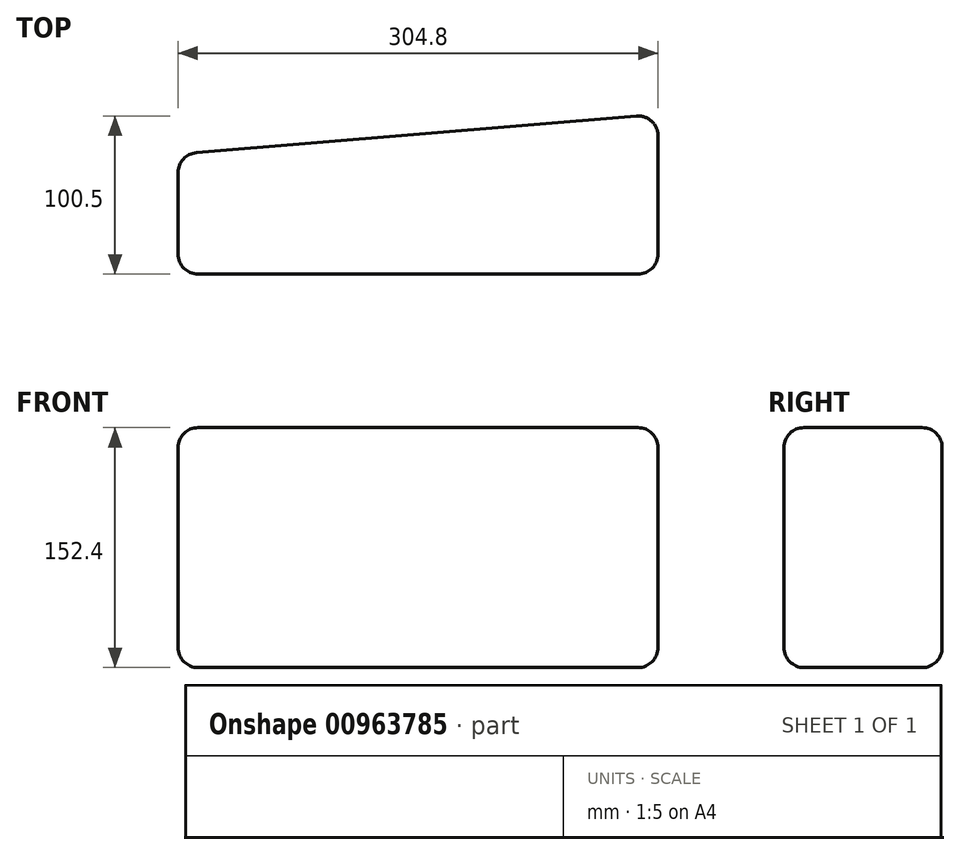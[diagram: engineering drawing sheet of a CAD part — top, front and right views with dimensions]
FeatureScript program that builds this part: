
annotation { "Feature Type Name" : "Feature", "Feature Type Description" : "" }
export const myFeature = defineFeature(function(context is Context, id is Id, definition is map)
    precondition{}
    {
        {
            var Q0;
            Q0=qCreatedBy(makeId("Top.planeOp"),FACE);
            var sketch = newSketch(context, id + "F0", { "sketchPlane" : qUnion([Q0])});
            skLineSegment(sketch, "E0", {"start": v(0, 0) * mm, "end": v(0, 76.2) * mm});
            skLineSegment(sketch, "E1", {"start": v(0, 76.2) * mm, "end": v(304.8, 101.6) * mm});
            skLineSegment(sketch, "E2", {"start": v(304.8, 101.6) * mm, "end": v(304.8, 0) * mm});
            skLineSegment(sketch, "E3", {"start": v(304.8, 0) * mm, "end": v(0, 0) * mm});
            skSolve(sketch);
        }
        {
            var Q0;
            Q0 = qSketchRegion(id + "F0", true);
            extrude(context, id + "F1", {"entities" : qUnion([Q0]), "depth" : 152.4 * mm, "offsetDistance" : 25.4 * mm});
        }
        {
            var Q0;
            Q0=makeQuery(id+"F1.opExtrude","CAP_EDGE",EDGE,{"disambiguationData":[OSD([sQuery(id+"F0.wireOp",EDGE,"E2")])],"isStart":false});
            var Q1;
            Q1=makeQuery(id+"F1.opExtrude","SWEPT_EDGE",EDGE,{"disambiguationData":[OSD([sQuery(id+"F0.wireOp",EDGE,"E0"),sQuery(id+"F0.wireOp",EDGE,"E1")])]});
            var Q2;
            Q2=makeQuery(id+"F1.opExtrude","CAP_EDGE",EDGE,{"disambiguationData":[OSD([sQuery(id+"F0.wireOp",EDGE,"E1")])],"isStart":false});
            var Q3;
            Q3=makeQuery(id+"F1.opExtrude","CAP_EDGE",EDGE,{"disambiguationData":[OSD([sQuery(id+"F0.wireOp",EDGE,"E0")])],"isStart":false});
            var Q4;
            Q4=makeQuery(id+"F1.opExtrude","SWEPT_EDGE",EDGE,{"disambiguationData":[OSD([sQuery(id+"F0.wireOp",EDGE,"E2"),sQuery(id+"F0.wireOp",EDGE,"E3")])]});
            var Q5;
            Q5=makeQuery(id+"F1.opExtrude","CAP_EDGE",EDGE,{"disambiguationData":[OSD([sQuery(id+"F0.wireOp",EDGE,"E3")])],"isStart":false});
            var Q6;
            Q6=makeQuery(id+"F1.opExtrude","SWEPT_EDGE",EDGE,{"disambiguationData":[OSD([sQuery(id+"F0.wireOp",EDGE,"E1"),sQuery(id+"F0.wireOp",EDGE,"E2")])]});
            var Q7;
            Q7=makeQuery(id+"F1.opExtrude","CAP_EDGE",EDGE,{"disambiguationData":[OSD([sQuery(id+"F0.wireOp",EDGE,"E2")])],"isStart":true});
            var Q8;
            Q8=makeQuery(id+"F1.opExtrude","SWEPT_EDGE",EDGE,{"disambiguationData":[OSD([sQuery(id+"F0.wireOp",EDGE,"E0"),sQuery(id+"F0.wireOp",EDGE,"E3")])]});
            var Q9;
            Q9=makeQuery(id+"F1.opExtrude","CAP_EDGE",EDGE,{"disambiguationData":[OSD([sQuery(id+"F0.wireOp",EDGE,"E0")])],"isStart":true});
            var Q10;
            Q10=makeQuery(id+"F1.opExtrude","CAP_EDGE",EDGE,{"disambiguationData":[OSD([sQuery(id+"F0.wireOp",EDGE,"E3")])],"isStart":true});
            var Q11;
            Q11=makeQuery(id+"F1.opExtrude","CAP_EDGE",EDGE,{"disambiguationData":[OSD([sQuery(id+"F0.wireOp",EDGE,"E1")])],"isStart":true});
            fillet(context, id + "F2", {"entities" : qUnion([Q0, Q1, Q2, Q3, Q4, Q5, Q6, Q7, Q8, Q9, Q10, Q11]), "tangentPropagation" : true, "radius" : 12.7 * mm, "defaultsChanged" : true, "vertexSettings" : [], "allowEdgeOverflow" : false});
        }
    });
